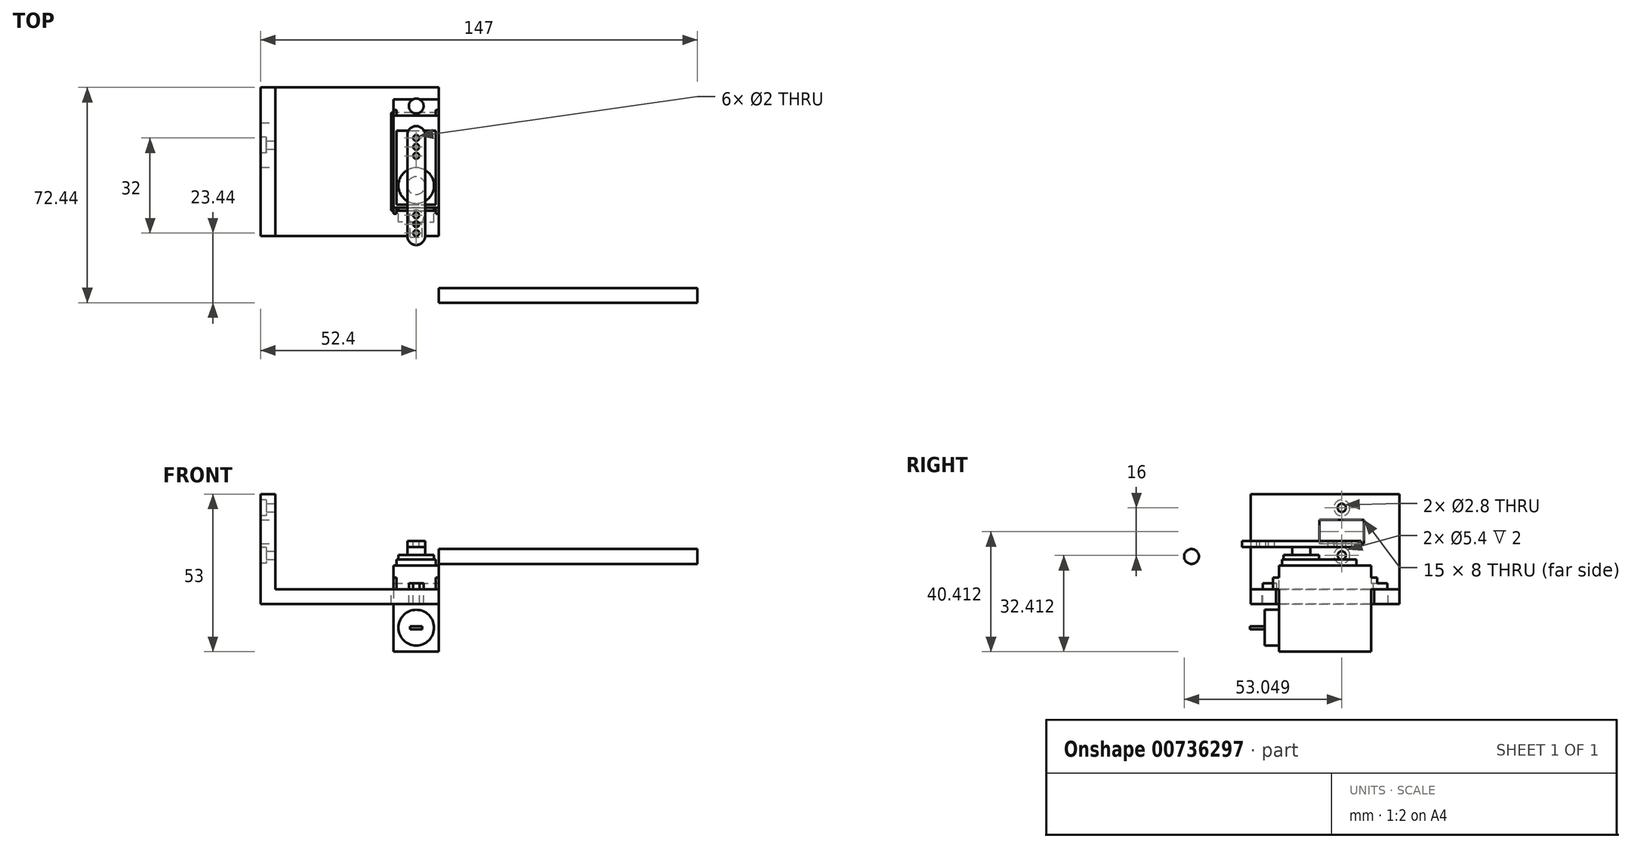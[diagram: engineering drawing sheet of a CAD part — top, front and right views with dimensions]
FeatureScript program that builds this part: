
annotation { "Feature Type Name" : "Feature", "Feature Type Description" : "" }
export const myFeature = defineFeature(function(context is Context, id is Id, definition is map)
    precondition{}
    {
        {
            var Q0;
            Q0=qCreatedBy(makeId("Top.planeOp"),FACE);
            var sketch = newSketch(context, id + "F0", { "sketchPlane" : qUnion([Q0])});
            skLineSegment(sketch, "E0.bottom", {"start": v(-15.2, 31) * mm, "end": v(0, 31) * mm});
            skLineSegment(sketch, "E0.top", {"start": v(-15.2, 0) * mm, "end": v(0, 0) * mm});
            skLineSegment(sketch, "E0.left", {"start": v(-15.2, 31) * mm, "end": v(-15.2, 0) * mm});
            skLineSegment(sketch, "E0.right", {"start": v(0, 31) * mm, "end": v(0, 0) * mm});
            skSolve(sketch);
        }
        {
            var Q0;
            Q0 = qSketchRegion(id + "F0", true);
            extrude(context, id + "F1", {"entities" : qUnion([Q0]), "depth" : 21 * mm, "offsetDistance" : 25 * mm});
        }
        {
            var Q0;
            Q0=makeQuery(id+"F1.opExtrude","CAP_FACE",FACE,{"disambiguationData":[OSD([sQuery(id+"F0.wireOp",EDGE,"E0.bottom"),sQuery(id+"F0.wireOp",EDGE,"E0.top"),sQuery(id+"F0.wireOp",EDGE,"E0.left"),sQuery(id+"F0.wireOp",EDGE,"E0.right")])],"isStart":false});
            var sketch = newSketch(context, id + "F2", { "sketchPlane" : qUnion([Q0])});
            skLineSegment(sketch, "E1.bottom", {"start": v(-15.2, 36.5) * mm, "end": v(0, 36.5) * mm});
            skLineSegment(sketch, "E1.top", {"start": v(-15.2, -5.5) * mm, "end": v(0, -5.5) * mm});
            skLineSegment(sketch, "E2.0", {"start": v(-15.2, 31) * mm, "end": v(-15.2, 0) * mm});
            skLineSegment(sketch, "E2.1", {"start": v(0, 31) * mm, "end": v(0, 0) * mm});
            skLineSegment(sketch, "E3", {"start": v(-15.2, 31) * mm, "end": v(-15.2, 36.5) * mm});
            skLineSegment(sketch, "E4", {"start": v(0, 31) * mm, "end": v(0, 36.5) * mm});
            skLineSegment(sketch, "E5", {"start": v(0, 0) * mm, "end": v(0, -5.5) * mm});
            skLineSegment(sketch, "E6", {"start": v(-15.2, 0) * mm, "end": v(-15.2, -5.5) * mm});
            skSolve(sketch);
        }
        {
            var Q0;
            Q0 = qSketchRegion(id + "F2", true);
            extrude(context, id + "F3", {"entities" : qUnion([Q0]), "operationType" : NewBodyOperationType.ADD, "depth" : 2 * mm, "offsetDistance" : 25 * mm});
        }
        {
            var Q0;
            Q0=makeQuery(id+"F3.opExtrude","CAP_FACE",FACE,{"disambiguationData":[OSD([sQuery(id+"F2.wireOp",EDGE,"E1.bottom"),sQuery(id+"F2.wireOp",EDGE,"E1.top"),sQuery(id+"F2.wireOp",EDGE,"E2.0"),sQuery(id+"F2.wireOp",EDGE,"E2.1"),sQuery(id+"F2.wireOp",EDGE,"E3"),sQuery(id+"F2.wireOp",EDGE,"E4"),sQuery(id+"F2.wireOp",EDGE,"E5"),sQuery(id+"F2.wireOp",EDGE,"E6")])],"isStart":false});
            var sketch = newSketch(context, id + "F4", { "sketchPlane" : qUnion([Q0])});
            skLineSegment(sketch, "E7.0", {"start": v(-15.2, 31) * mm, "end": v(0, 31) * mm});
            skLineSegment(sketch, "E8.bottom", {"start": v(-15.2, 31) * mm, "end": v(-14.2, 31) * mm});
            skLineSegment(sketch, "E8.top", {"start": v(-15.2, 33) * mm, "end": v(-14.2, 33) * mm});
            skLineSegment(sketch, "E8.left", {"start": v(-15.2, 31) * mm, "end": v(-15.2, 33) * mm});
            skLineSegment(sketch, "E8.right", {"start": v(-14.2, 31) * mm, "end": v(-14.2, 33) * mm});
            skLineSegment(sketch, "E9.0", {"start": v(-15.2, 0) * mm, "end": v(0, 0) * mm});
            skLineSegment(sketch, "E10", {"start": v(-7.6, 31) * mm, "end": v(-7.6, 0) * mm, "construction": true});
            skLineSegment(sketch, "E11.MirrorCS", {"start": v(0, 31) * mm, "end": v(-1, 31) * mm});
            skLineSegment(sketch, "E12.MirrorCS", {"start": v(-1, 31) * mm, "end": v(-1, 33) * mm});
            skLineSegment(sketch, "E13.MirrorCS", {"start": v(0, 31) * mm, "end": v(0, 33) * mm});
            skLineSegment(sketch, "E14.MirrorCS", {"start": v(0, 33) * mm, "end": v(-1, 33) * mm});
            skLineSegment(sketch, "E15", {"start": v(-15.2, 15.5) * mm, "end": v(0, 15.5) * mm, "construction": true});
            skLineSegment(sketch, "E16.MirrorCS", {"start": v(0, 0) * mm, "end": v(-1, 0) * mm});
            skLineSegment(sketch, "E17.MirrorCS", {"start": v(-15.2, 0) * mm, "end": v(-14.2, 0) * mm});
            skLineSegment(sketch, "E18.MirrorCS", {"start": v(-1, 0) * mm, "end": v(-1, -2) * mm});
            skLineSegment(sketch, "E19.MirrorCS", {"start": v(0, 0) * mm, "end": v(0, -2) * mm});
            skLineSegment(sketch, "E20.MirrorCS", {"start": v(0, -2) * mm, "end": v(-1, -2) * mm});
            skLineSegment(sketch, "E21.MirrorCS", {"start": v(-14.2, 0) * mm, "end": v(-14.2, -2) * mm});
            skLineSegment(sketch, "E22.MirrorCS", {"start": v(-15.2, -2) * mm, "end": v(-14.2, -2) * mm});
            skLineSegment(sketch, "E23.MirrorCS", {"start": v(-15.2, 0) * mm, "end": v(-15.2, -2) * mm});
            skCircle(sketch, "E24", {"center": v(-7.6, 34.25) * mm, "radius": 2.5 * mm});
            skLineSegment(sketch, "E25", {"start": v(-7.6, 36.5) * mm, "end": v(-7.6, 34.25) * mm, "construction": true});
            skCircle(sketch, "E26.MirrorC", {"center": v(-7.6, -3.25) * mm, "radius": 2.5 * mm});
            skSolve(sketch);
        }
        {
            var Q0;
            {var subQ0=sQuery(id+"F4.wireOp",EDGE,"E24");var subQ1=makeQuery(id+"F3.opExtrude","CAP_EDGE",EDGE,{"disambiguationData":[OSD([sQuery(id+"F2.wireOp",EDGE,"E1.bottom")])],"isStart":false});var subQ2=makeQuery(id+"F4.imprint","INTERSECT",VERTEX,{"disambiguationData":[OD(0.0)],"derivedFrom":[subQ1,subQ0]});Q0=qUnion([makeQuery(id+"F4.imprint","IMPRINT",FACE,{"disambiguationData":[TD([[makeQuery(id+"F4.imprint","IMPRINT",EDGE,{"disambiguationData":[TD([[subQ2,1.0]])],"derivedFrom":subQ0}),1.0]])]}),makeQuery(id+"F4.imprint","IMPRINT",FACE,{"disambiguationData":[TD([[makeQuery(id+"F4.imprint","IMPRINT",EDGE,{"disambiguationData":[TD([[subQ2,-1.0]])],"derivedFrom":subQ0}),1.0]])]})]);}
            var Q1;
            {var subQ0=sQuery(id+"F4.wireOp",EDGE,"E26.MirrorC");var subQ1=makeQuery(id+"F3.opExtrude","CAP_EDGE",EDGE,{"disambiguationData":[OSD([sQuery(id+"F2.wireOp",EDGE,"E1.top")])],"isStart":false});var subQ2=makeQuery(id+"F4.imprint","INTERSECT",VERTEX,{"disambiguationData":[OD(0.0)],"derivedFrom":[subQ1,subQ0]});Q1=qUnion([makeQuery(id+"F4.imprint","IMPRINT",FACE,{"disambiguationData":[TD([[makeQuery(id+"F4.imprint","IMPRINT",EDGE,{"disambiguationData":[TD([[subQ2,1.0]])],"derivedFrom":subQ0}),-1.0]])]}),makeQuery(id+"F4.imprint","IMPRINT",FACE,{"disambiguationData":[TD([[makeQuery(id+"F4.imprint","IMPRINT",EDGE,{"disambiguationData":[TD([[subQ2,-1.0]])],"derivedFrom":subQ0}),-1.0]])]})]);}
            extrude(context, id + "F5", {"entities" : qUnion([Q0, Q1]), "operationType" : NewBodyOperationType.REMOVE, "endBound" : BoundingType.UP_TO_NEXT, "oppositeDirection" : true, "depth" : 25 * mm, "offsetDistance" : 25 * mm});
        }
        {
            var Q0;
            Q0=makeQuery(id+"F4.imprint","IMPRINT",FACE,{"disambiguationData":[TD([[makeQuery(id+"F4.imprint","IMPRINT",EDGE,{"derivedFrom":sQuery(id+"F4.wireOp",EDGE,"E8.top")}),-1.0]])]});
            var Q1;
            {var subQ2=sQuery(id+"F4.wireOp",EDGE,"E12.MirrorCS");Q1=makeQuery(id+"F4.imprint","IMPRINT",FACE,{"disambiguationData":[TD([[makeQuery(id+"F4.imprint","IMPRINT",EDGE,{"derivedFrom":subQ2}),-1.0]])]});}
            var Q2;
            {var subQ2=sQuery(id+"F4.wireOp",EDGE,"E18.MirrorCS");Q2=makeQuery(id+"F4.imprint","IMPRINT",FACE,{"disambiguationData":[TD([[makeQuery(id+"F4.imprint","IMPRINT",EDGE,{"derivedFrom":subQ2}),1.0]])]});}
            var Q3;
            {var subQ0=sQuery(id+"F4.wireOp",EDGE,"E21.MirrorCS");Q3=makeQuery(id+"F4.imprint","IMPRINT",FACE,{"disambiguationData":[TD([[makeQuery(id+"F4.imprint","IMPRINT",EDGE,{"derivedFrom":subQ0}),-1.0]])]});}
            extrude(context, id + "F6", {"entities" : qUnion([Q0, Q1, Q2, Q3]), "operationType" : NewBodyOperationType.ADD, "depth" : 2 * mm, "offsetDistance" : 25 * mm});
        }
        {
            var Q0;
            {var subQ0=sQuery(id+"F4.wireOp",EDGE,"E7.0");var subQ7=makeQuery(id+"F4.imprint","INTERSECT",VERTEX,{"derivedFrom":[subQ0,sQuery(id+"F4.wireOp",EDGE,"E8.right")]});Q0=makeQuery(id+"F4.imprint","IMPRINT",FACE,{"disambiguationData":[TD([[makeQuery(id+"F4.imprint","IMPRINT",EDGE,{"disambiguationData":[TD([[subQ7,-1.0]])],"derivedFrom":subQ0}),-1.0]])]});}
            extrude(context, id + "F7", {"entities" : qUnion([Q0]), "operationType" : NewBodyOperationType.ADD, "depth" : 6 * mm, "offsetDistance" : 25 * mm});
        }
        {
            var Q0;
            Q0=makeQuery(id+"F7.opExtrude","CAP_FACE",FACE,{"disambiguationData":[OSD([sQuery(id+"F2.wireOp",EDGE,"E2.0"),sQuery(id+"F2.wireOp",EDGE,"E2.1"),sQuery(id+"F2.wireOp",EDGE,"E3"),sQuery(id+"F2.wireOp",EDGE,"E4"),sQuery(id+"F2.wireOp",EDGE,"E5"),sQuery(id+"F2.wireOp",EDGE,"E6"),sQuery(id+"F4.wireOp",EDGE,"E7.0"),sQuery(id+"F4.wireOp",EDGE,"E9.0")])],"isStart":false});
            var sketch = newSketch(context, id + "F8", { "sketchPlane" : qUnion([Q0])});
            skLineSegment(sketch, "E27.bottom", {"start": v(-14.2, 1) * mm, "end": v(-1, 1) * mm});
            skLineSegment(sketch, "E27.top", {"start": v(-14.2, 26) * mm, "end": v(-1, 26) * mm});
            skLineSegment(sketch, "E27.left", {"start": v(-14.2, 1) * mm, "end": v(-14.2, 26) * mm});
            skLineSegment(sketch, "E27.right", {"start": v(-1, 1) * mm, "end": v(-1, 26) * mm});
            skLineSegment(sketch, "E28", {"start": v(-7.6, 0) * mm, "end": v(-7.6, 1) * mm, "construction": true});
            skPoint(sketch, "E28.endSnap0", {"position": v(-7.6, 1) * mm});
            skCircle(sketch, "E29", {"center": v(-7.6, 7.5) * mm, "radius": 6 * mm});
            skLineSegment(sketch, "E30", {"start": v(-7.6, 0) * mm, "end": v(-7.6, 7.5) * mm, "construction": true});
            skSolve(sketch);
        }
        {
            var Q0;
            Q0=makeQuery(id+"F8.imprint","IMPRINT",FACE,{"disambiguationData":[TD([[makeQuery(id+"F8.imprint","IMPRINT",EDGE,{"derivedFrom":sQuery(id+"F8.wireOp",EDGE,"E29")}),1.0]])]});
            extrude(context, id + "F9", {"entities" : qUnion([Q0]), "operationType" : NewBodyOperationType.ADD, "depth" : 3.6 * mm, "offsetDistance" : 25 * mm});
        }
        {
            var Q0;
            Q0=makeQuery(id+"F8.imprint","IMPRINT",FACE,{"disambiguationData":[TD([[makeQuery(id+"F8.imprint","IMPRINT",EDGE,{"derivedFrom":sQuery(id+"F8.wireOp",EDGE,"E27.bottom")}),1.0]])]});
            extrude(context, id + "F10", {"entities" : qUnion([Q0]), "operationType" : NewBodyOperationType.ADD, "depth" : 2 * mm, "offsetDistance" : 25 * mm});
        }
        {
            var Q0;
            Q0=makeQuery(id+"F9.opExtrude","CAP_FACE",FACE,{"disambiguationData":[OSD([sQuery(id+"F8.wireOp",EDGE,"E29")])],"isStart":false});
            var sketch = newSketch(context, id + "F11", { "sketchPlane" : qUnion([Q0])});
            skCircle(sketch, "E31", {"center": v(-7.6, 7.5) * mm, "radius": 3 * mm});
            skSolve(sketch);
        }
        {
            var Q0;
            Q0 = qSketchRegion(id + "F11", true);
            extrude(context, id + "F12", {"entities" : qUnion([Q0]), "depth" : 2.6 * mm, "offsetDistance" : 25 * mm});
        }
        {
            var Q0;
            Q0=makeQuery(id+"F1.opExtrude","SWEPT_FACE",FACE,{"disambiguationData":[OSD([sQuery(id+"F0.wireOp",EDGE,"E0.top")])]});
            var sketch = newSketch(context, id + "F13", { "sketchPlane" : qUnion([Q0])});
            skLineSegment(sketch, "E32", {"start": v(-7.6, 21) * mm, "end": v(-7.6, 8.1) * mm, "construction": true});
            skCircle(sketch, "E33", {"center": v(-7.6, 8.1) * mm, "radius": 6 * mm});
            skSolve(sketch);
        }
        {
            var Q0;
            Q0 = qSketchRegion(id + "F13", true);
            extrude(context, id + "F14", {"entities" : qUnion([Q0]), "operationType" : NewBodyOperationType.ADD, "depth" : 4.8 * mm, "offsetDistance" : 25 * mm});
        }
        {
            var Q0;
            Q0=makeQuery(id+"F14.opExtrude","CAP_FACE",FACE,{"disambiguationData":[OSD([sQuery(id+"F13.wireOp",EDGE,"E33")])],"isStart":false});
            var sketch = newSketch(context, id + "F15", { "sketchPlane" : qUnion([Q0])});
            skLineSegment(sketch, "E34.bottom", {"start": v(-9.6, 8.6) * mm, "end": v(-5.6, 8.6) * mm});
            skLineSegment(sketch, "E34.top", {"start": v(-9.6, 7.6) * mm, "end": v(-5.6, 7.6) * mm});
            skLineSegment(sketch, "E34.left", {"start": v(-9.6, 8.6) * mm, "end": v(-9.6, 7.6) * mm});
            skLineSegment(sketch, "E34.right", {"start": v(-5.6, 8.6) * mm, "end": v(-5.6, 7.6) * mm});
            skLineSegment(sketch, "E35", {"start": v(-7.6, 7.6) * mm, "end": v(-7.6, 8.6) * mm, "construction": true});
            skPoint(sketch, "E36", {"position": v(-7.6, 8.1) * mm});
            skSolve(sketch);
        }
        {
            var Q0;
            Q0 = qSketchRegion(id + "F15", true);
            extrude(context, id + "F16", {"entities" : qUnion([Q0]), "operationType" : NewBodyOperationType.ADD, "depth" : 5 * mm, "offsetDistance" : 25 * mm});
        }
        {
            var Q0;
            Q0=makeQuery(id+"F12.opExtrude","CAP_FACE",FACE,{"disambiguationData":[OSD([sQuery(id+"F11.wireOp",EDGE,"E31")])],"isStart":false});
            var sketch = newSketch(context, id + "F17", { "sketchPlane" : qUnion([Q0])});
            skLineSegment(sketch, "E37", {"start": v(-10.6, 24.5) * mm, "end": v(-10.6, -9.5) * mm});
            skLineSegment(sketch, "E38", {"start": v(-7.6, -12.5) * mm, "end": v(-7.6, -12.5) * mm});
            skPoint(sketch, "E39", {"position": v(0, 9.77) * mm});
            skLineSegment(sketch, "E40", {"start": v(-7.6, 27.5) * mm, "end": v(-7.6, 27.5) * mm});
            skLineSegment(sketch, "E41", {"start": v(-4.6, 24.5) * mm, "end": v(-4.6, -9.5) * mm});
            skPoint(sketch, "E42", {"position": v(-4.6, 7.5) * mm});
            skPoint(sketch, "E43.visualSharp", {"position": v(-10.6, 27.5) * mm});
            skArc(sketch, "E43.filletArc", {"start": v(-7.6, 27.5) * mm, "mid": v(-9.72, 26.62) * mm, "end": v(-10.6, 24.5) * mm});
            skPoint(sketch, "E44.visualSharp", {"position": v(-4.6, 27.5) * mm});
            skArc(sketch, "E44.filletArc", {"start": v(-4.6, 24.5) * mm, "mid": v(-5.48, 26.62) * mm, "end": v(-7.6, 27.5) * mm});
            skPoint(sketch, "E45.visualSharp", {"position": v(-4.6, -12.5) * mm});
            skArc(sketch, "E45.filletArc", {"start": v(-7.6, -12.5) * mm, "mid": v(-5.48, -11.62) * mm, "end": v(-4.6, -9.5) * mm});
            skPoint(sketch, "E46.visualSharp", {"position": v(-10.6, -12.5) * mm});
            skArc(sketch, "E46.filletArc", {"start": v(-10.6, -9.5) * mm, "mid": v(-9.72, -11.62) * mm, "end": v(-7.6, -12.5) * mm});
            skSolve(sketch);
        }
        {
            var Q0;
            Q0 = qSketchRegion(id + "F17", true);
            extrude(context, id + "F18", {"entities" : qUnion([Q0]), "operationType" : NewBodyOperationType.ADD, "depth" : 2 * mm, "offsetDistance" : 25 * mm});
        }
        {
            var Q0;
            Q0=makeQuery(id+"F18.opExtrude","CAP_FACE",FACE,{"disambiguationData":[OSD([sQuery(id+"F17.wireOp",EDGE,"E37"),sQuery(id+"F17.wireOp",EDGE,"E41"),sQuery(id+"F17.wireOp",EDGE,"E43.filletArc"),sQuery(id+"F17.wireOp",EDGE,"E44.filletArc"),sQuery(id+"F17.wireOp",EDGE,"E45.filletArc"),sQuery(id+"F17.wireOp",EDGE,"E46.filletArc")])],"isStart":false});
            var sketch = newSketch(context, id + "F19", { "sketchPlane" : qUnion([Q0])});
            skCircle(sketch, "E47", {"center": v(-7.6, 23.5) * mm, "radius": 1 * mm});
            skLineSegment(sketch, "E48", {"start": v(-7.6, -12.5) * mm, "end": v(-7.6, 27.5) * mm, "construction": true});
            skLineSegment(sketch, "E49", {"start": v(-4.6, 7.5) * mm, "end": v(-10.6, 7.5) * mm, "construction": true});
            skCircle(sketch, "E50.MirrorC", {"center": v(-7.6, -8.5) * mm, "radius": 1 * mm});
            skLineSegment(sketch, "E51", {"start": v(-7.6, 23.5) * mm, "end": v(-7.6, 27.5) * mm, "construction": true});
            skCircle(sketch, "E52.0.1.0", {"center": v(-7.6, 20.5) * mm, "radius": 1 * mm});
            skCircle(sketch, "E52.0.2.0", {"center": v(-7.6, 17.5) * mm, "radius": 1 * mm});
            skLineSegment(sketch, "E52.direction1", {"start": v(-7.6, 23.5) * mm, "end": v(-5.27, 23.5) * mm, "construction": true});
            skLineSegment(sketch, "E52.direction2", {"start": v(-7.6, 23.5) * mm, "end": v(-7.6, 20.5) * mm, "construction": true});
            skCircle(sketch, "E53.MirrorC", {"center": v(-7.6, -2.5) * mm, "radius": 1 * mm});
            skCircle(sketch, "E54.MirrorC", {"center": v(-7.6, -5.5) * mm, "radius": 1 * mm});
            skSolve(sketch);
        }
        {
            var Q0;
            Q0 = qSketchRegion(id + "F19", true);
            extrude(context, id + "F20", {"entities" : qUnion([Q0]), "operationType" : NewBodyOperationType.REMOVE, "endBound" : BoundingType.UP_TO_NEXT, "oppositeDirection" : true, "depth" : 25 * mm, "offsetDistance" : 25 * mm});
        }
        {
            var Q0;
            {var subQ0=sQuery(id+"F2.wireOp",EDGE,"E1.top");var subQ1=sQuery(id+"F2.wireOp",EDGE,"E6");var subQ2=sQuery(id+"F2.wireOp",EDGE,"E3");var subQ3=sQuery(id+"F2.wireOp",EDGE,"E2.0");var subQ4=sQuery(id+"F2.wireOp",EDGE,"E5");var subQ5=sQuery(id+"F2.wireOp",EDGE,"E4");var subQ6=sQuery(id+"F2.wireOp",EDGE,"E2.1");Q0=makeQuery(id+"F3.boolean.opBoolean","SPLIT",FACE,{"disambiguationData":[TD([makeQuery(id+"F1.opExtrude","SWEPT_FACE",FACE,{"disambiguationData":[OSD([sQuery(id+"F0.wireOp",EDGE,"E0.top")])]})])],"derivedFrom":makeQuery(id+"F3.opExtrude","CAP_FACE",FACE,{"disambiguationData":[OSD([sQuery(id+"F2.wireOp",EDGE,"E1.bottom"),subQ0,subQ3,subQ6,subQ2,subQ5,subQ4,subQ1])],"isStart":true})});}
            var sketch = newSketch(context, id + "F21", { "sketchPlane" : qUnion([Q0])});
            skLineSegment(sketch, "E55.bottom", {"start": v(0, 9.5) * mm, "end": v(-60, 9.5) * mm});
            skLineSegment(sketch, "E55.top", {"start": v(0, -40.5) * mm, "end": v(-60, -40.5) * mm});
            skLineSegment(sketch, "E55.right", {"start": v(-60, 9.5) * mm, "end": v(-60, -40.5) * mm});
            skCircle(sketch, "E56.0", {"center": v(-7.6, 3.25) * mm, "radius": 2.5 * mm});
            skCircle(sketch, "E57.0", {"center": v(-7.6, -34.25) * mm, "radius": 2.5 * mm});
            skPoint(sketch, "E58", {"position": v(0, -15.5) * mm});
            skLineSegment(sketch, "E59", {"start": v(0, -40.5) * mm, "end": v(0, -32) * mm});
            skLineSegment(sketch, "E60", {"start": v(0, -32) * mm, "end": v(-16, -32) * mm});
            skLineSegment(sketch, "E61", {"start": v(-16, -32) * mm, "end": v(-16, 1) * mm});
            skLineSegment(sketch, "E62", {"start": v(-16, 1) * mm, "end": v(0, 1) * mm});
            skLineSegment(sketch, "E63", {"start": v(0, 1) * mm, "end": v(0, 9.5) * mm});
            skPoint(sketch, "E64", {"position": v(0, -36.5) * mm});
            skSolve(sketch);
        }
        {
            var Q0;
            {var subQ20=sQuery(id+"F21.wireOp",EDGE,"E55.bottom");Q0=makeQuery(id+"F21.imprint","IMPRINT",FACE,{"disambiguationData":[TD([[makeQuery(id+"F21.imprint","IMPRINT",EDGE,{"derivedFrom":subQ20}),1.0]])]});}
            var Q1;
            {var subQ5=sQuery(id+"F2.wireOp",EDGE,"E1.top");var subQ8=makeQuery(id+"F1.opExtrude","SWEPT_FACE",FACE,{"disambiguationData":[OSD([sQuery(id+"F0.wireOp",EDGE,"E0.right")])]});var subQ9=makeQuery(id+"F5.boolean.opBoolean","SPLIT",EDGE,{"disambiguationData":[TD([subQ8])],"derivedFrom":makeQuery(id+"F3.opExtrude","CAP_EDGE",EDGE,{"disambiguationData":[OSD([subQ5])],"isStart":true})});Q1=makeQuery(id+"F21.imprint","IMPRINT",FACE,{"disambiguationData":[TD([[makeQuery(id+"F21.imprint","IMPRINT",EDGE,{"derivedFrom":subQ9}),-1.0]])]});}
            var Q2;
            {var subQ5=sQuery(id+"F2.wireOp",EDGE,"E1.top");var subQ7=makeQuery(id+"F1.opExtrude","SWEPT_FACE",FACE,{"disambiguationData":[OSD([sQuery(id+"F0.wireOp",EDGE,"E0.left")])]});var subQ9=makeQuery(id+"F5.boolean.opBoolean","SPLIT",EDGE,{"disambiguationData":[TD([subQ7])],"derivedFrom":makeQuery(id+"F3.opExtrude","CAP_EDGE",EDGE,{"disambiguationData":[OSD([subQ5])],"isStart":true})});Q2=makeQuery(id+"F21.imprint","IMPRINT",FACE,{"disambiguationData":[TD([[makeQuery(id+"F21.imprint","IMPRINT",EDGE,{"derivedFrom":subQ9}),-1.0]])]});}
            extrude(context, id + "F22", {"entities" : qUnion([Q0, Q1, Q2]), "depth" : 5 * mm, "offsetDistance" : 25 * mm});
        }
        {
            var Q0;
            Q0=makeQuery(id+"F22.opExtrude","CAP_FACE",FACE,{"disambiguationData":[OSD([sQuery(id+"F21.wireOp",EDGE,"E55.bottom"),sQuery(id+"F21.wireOp",EDGE,"E55.top"),sQuery(id+"F21.wireOp",EDGE,"E55.left"),sQuery(id+"F21.wireOp",EDGE,"E55.right"),sQuery(id+"F21.wireOp",EDGE,"E56.0"),sQuery(id+"F21.wireOp",EDGE,"E57.0")])],"isStart":true});
            var sketch = newSketch(context, id + "F23", { "sketchPlane" : qUnion([Q0])});
            skLineSegment(sketch, "E65.0", {"start": v(-60, -9.5) * mm, "end": v(-60, 40.5) * mm});
            skLineSegment(sketch, "E66", {"start": v(-60, -9.5) * mm, "end": v(-55, -9.5) * mm});
            skLineSegment(sketch, "E67", {"start": v(-55, -9.5) * mm, "end": v(-55, 40.5) * mm});
            skLineSegment(sketch, "E68", {"start": v(-55, 40.5) * mm, "end": v(-60, 40.5) * mm});
            skSolve(sketch);
        }
        {
            var Q0;
            Q0 = qSketchRegion(id + "F23", true);
            extrude(context, id + "F24", {"entities" : qUnion([Q0]), "operationType" : NewBodyOperationType.ADD, "depth" : 32 * mm, "offsetDistance" : 25 * mm});
        }
        {
            var Q0;
            Q0=makeQuery(id+"F24.opExtrude","SWEPT_FACE",FACE,{"disambiguationData":[OSD([sQuery(id+"F23.wireOp",EDGE,"E67")])]});
            var sketch = newSketch(context, id + "F25", { "sketchPlane" : qUnion([Q0])});
            skCircle(sketch, "E69", {"center": v(21.1, 48.41) * mm, "radius": 1.4 * mm});
            skCircle(sketch, "E70", {"center": v(21.1, 32.41) * mm, "radius": 1.4 * mm});
            skLineSegment(sketch, "E71", {"start": v(21.1, 48.41) * mm, "end": v(21.1, 32.41) * mm, "construction": true});
            skLineSegment(sketch, "E72.0", {"start": v(22.5, 37.2) * mm, "end": v(24.5, 37.2) * mm});
            skLineSegment(sketch, "E73.bottom", {"start": v(13.6, 36.41) * mm, "end": v(28.6, 36.41) * mm});
            skLineSegment(sketch, "E73.top", {"start": v(13.6, 44.41) * mm, "end": v(28.6, 44.41) * mm});
            skLineSegment(sketch, "E73.left", {"start": v(13.6, 36.41) * mm, "end": v(13.6, 44.41) * mm});
            skLineSegment(sketch, "E73.right", {"start": v(28.6, 36.41) * mm, "end": v(28.6, 44.41) * mm});
            skPoint(sketch, "E73.middle", {"position": v(21.1, 40.41) * mm});
            skSolve(sketch);
        }
        {
            var Q0;
            Q0 = qSketchRegion(id + "F25", true);
            extrude(context, id + "F26", {"entities" : qUnion([Q0]), "operationType" : NewBodyOperationType.REMOVE, "endBound" : BoundingType.UP_TO_NEXT, "oppositeDirection" : true, "depth" : 25 * mm, "offsetDistance" : 25 * mm});
        }
        {
            var Q0;
            Q0=makeQuery(id+"F24.boolean.opBoolean","MERGE",FACE,{"derivedFrom":[makeQuery(id+"F22.opExtrude","SWEPT_FACE",FACE,{"disambiguationData":[OSD([sQuery(id+"F21.wireOp",EDGE,"E55.right")])]}),makeQuery(id+"F24.opExtrude","SWEPT_FACE",FACE,{"disambiguationData":[OSD([sQuery(id+"F23.wireOp",EDGE,"E65.0")])]})]});
            var sketch = newSketch(context, id + "F27", { "sketchPlane" : qUnion([Q0])});
            skCircle(sketch, "E74", {"center": v(-21.1, 32.41) * mm, "radius": 2.7 * mm});
            skCircle(sketch, "E75", {"center": v(-21.1, 48.41) * mm, "radius": 2.7 * mm});
            skSolve(sketch);
        }
        {
            var Q0;
            Q0 = qSketchRegion(id + "F27", true);
            extrude(context, id + "F28", {"entities" : qUnion([Q0]), "operationType" : NewBodyOperationType.REMOVE, "oppositeDirection" : true, "depth" : 2 * mm, "offsetDistance" : 25 * mm});
        }
        {
            var Q0;
            Q0=qCreatedBy(makeId("Right.planeOp"),FACE);
            var sketch = newSketch(context, id + "F29", { "sketchPlane" : qUnion([Q0])});
            skCircle(sketch, "E76", {"center": v(-29.44, 32.04) * mm, "radius": 2.5 * mm});
            skSolve(sketch);
        }
        {
            var Q0;
            Q0 = qSketchRegion(id + "F29", true);
            extrude(context, id + "F30", {"entities" : qUnion([Q0]), "depth" : 87 * mm, "offsetDistance" : 25 * mm});
        }
    });
